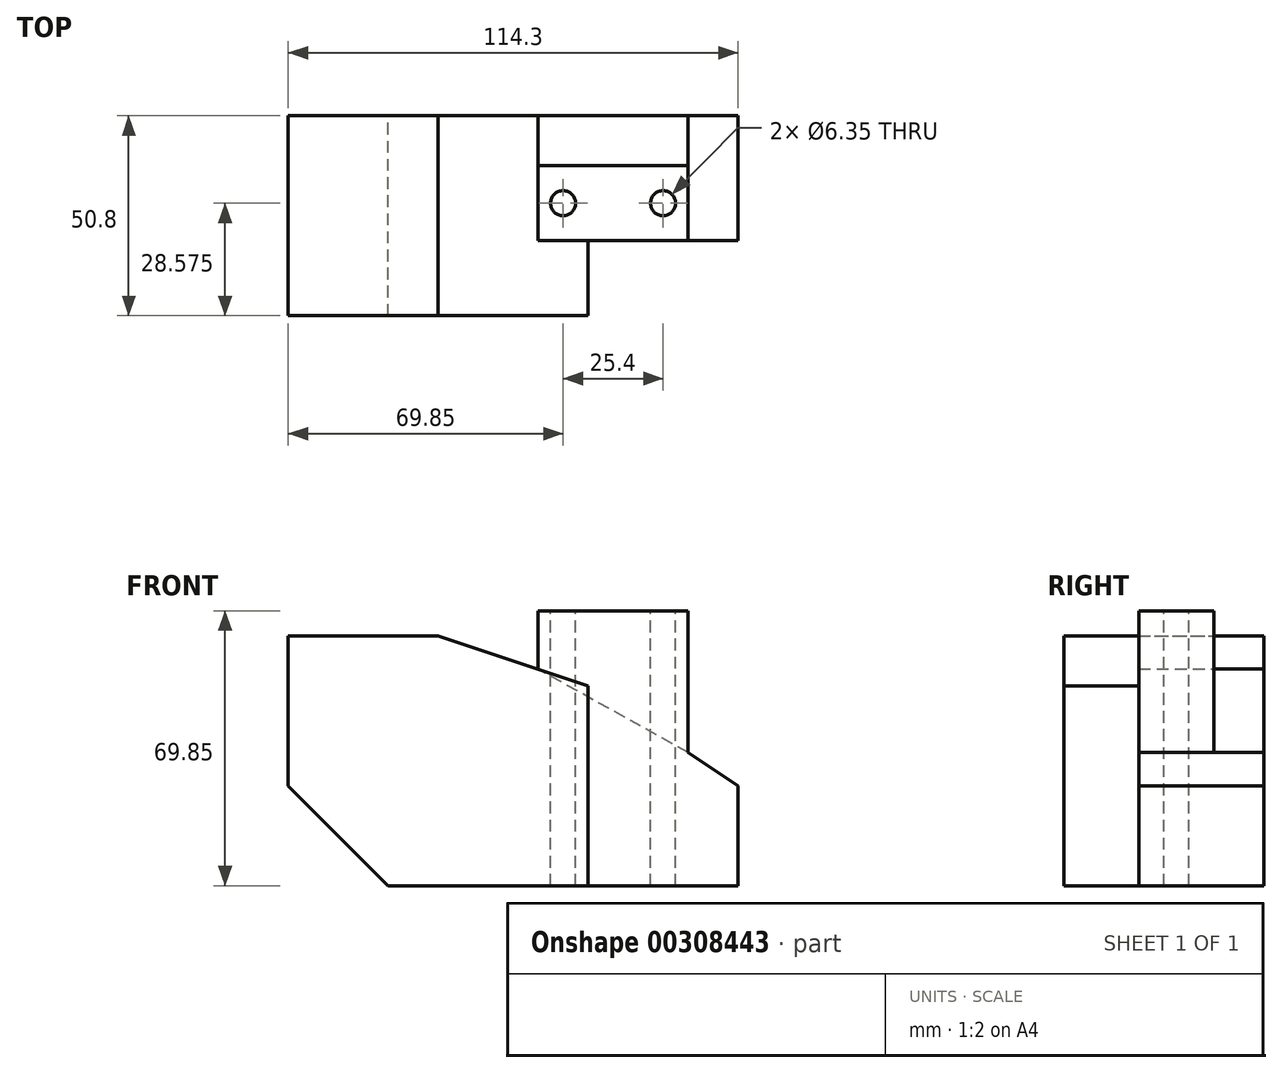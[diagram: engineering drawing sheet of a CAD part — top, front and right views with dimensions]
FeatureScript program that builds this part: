
annotation { "Feature Type Name" : "Feature", "Feature Type Description" : "" }
export const myFeature = defineFeature(function(context is Context, id is Id, definition is map)
    precondition{}
    {
        {
            var Q0;
            Q0=qCreatedBy(makeId("Front.planeOp"),FACE);
            var sketch = newSketch(context, id + "F0", { "sketchPlane" : qUnion([Q0])});
            skLineSegment(sketch, "E0.bottom", {"start": v(25.4, 0) * mm, "end": v(76.2, 0) * mm});
            skLineSegment(sketch, "E0.top", {"start": v(0, 63.5) * mm, "end": v(38.1, 63.5) * mm});
            skLineSegment(sketch, "E0.left", {"start": v(0, 25.4) * mm, "end": v(0, 63.5) * mm});
            skLineSegment(sketch, "E0.right", {"start": v(76.2, 0) * mm, "end": v(76.2, 50.8) * mm});
            skLineSegment(sketch, "E1", {"start": v(38.1, 63.5) * mm, "end": v(76.2, 50.8) * mm});
            skPoint(sketch, "E2.orphan", {"position": v(76.2, 63.5) * mm});
            skLineSegment(sketch, "E3", {"start": v(0, 25.4) * mm, "end": v(25.4, 0) * mm});
            skPoint(sketch, "E4.orphan", {"position": v(0, 0) * mm});
            skSolve(sketch);
        }
        {
            var Q0;
            Q0 = qSketchRegion(id + "F0", true);
            extrude(context, id + "F1", {"entities" : qUnion([Q0]), "depth" : 50.8 * mm});
        }
        {
            var Q0;
            Q0=qCreatedBy(makeId("Front.planeOp"),FACE);
            var sketch = newSketch(context, id + "F2", { "sketchPlane" : qUnion([Q0])});
            skLineSegment(sketch, "E5", {"start": v(63.5, 55.03) * mm, "end": v(63.5, 69.85) * mm});
            skLineSegment(sketch, "E6", {"start": v(63.5, 69.85) * mm, "end": v(101.6, 69.85) * mm});
            skLineSegment(sketch, "E7", {"start": v(101.6, 69.85) * mm, "end": v(101.6, 31.75) * mm});
            skLineSegment(sketch, "E8", {"start": v(101.6, 31.75) * mm, "end": v(76.2, 31.75) * mm});
            skLineSegment(sketch, "E9", {"start": v(76.2, 31.75) * mm, "end": v(76.2, 50.8) * mm});
            skLineSegment(sketch, "E10", {"start": v(76.2, 50.8) * mm, "end": v(63.5, 55.03) * mm});
            skSolve(sketch);
        }
        {
            var Q0;
            Q0 = qSketchRegion(id + "F2", true);
            extrude(context, id + "F3", {"entities" : qUnion([Q0]), "operationType" : NewBodyOperationType.ADD, "depth" : 31.75 * mm});
        }
        {
            var Q0;
            Q0=qCreatedBy(makeId("Front.planeOp"),FACE);
            var sketch = newSketch(context, id + "F4", { "sketchPlane" : qUnion([Q0])});
            skLineSegment(sketch, "E11", {"start": v(76.2, 50.8) * mm, "end": v(114.3, 25.4) * mm});
            skLineSegment(sketch, "E12", {"start": v(76.2, 0) * mm, "end": v(114.3, 0) * mm});
            skLineSegment(sketch, "E13", {"start": v(114.3, 0) * mm, "end": v(114.3, 25.4) * mm});
            skLineSegment(sketch, "E14", {"start": v(76.2, 50.8) * mm, "end": v(76.2, 0) * mm});
            skSolve(sketch);
        }
        {
            var Q0;
            Q0 = qSketchRegion(id + "F4", true);
            extrude(context, id + "F5", {"entities" : qUnion([Q0]), "operationType" : NewBodyOperationType.ADD, "depth" : 31.75 * mm});
        }
        {
            var Q0;
            Q0=makeQuery(id+"F5.boolean.opBoolean","MERGE",FACE,{"derivedFrom":[makeQuery(id+"F3.boolean.opBoolean","MERGE",FACE,{"derivedFrom":[makeQuery(id+"F1.opExtrude","CAP_FACE",FACE,{"disambiguationData":[OSD([sQuery(id+"F0.wireOp",EDGE,"E0.bottom"),sQuery(id+"F0.wireOp",EDGE,"E0.top"),sQuery(id+"F0.wireOp",EDGE,"E0.left"),sQuery(id+"F0.wireOp",EDGE,"E0.right"),sQuery(id+"F0.wireOp",EDGE,"E1"),sQuery(id+"F0.wireOp",EDGE,"E3")])],"isStart":true}),makeQuery(id+"F3.opExtrude","CAP_FACE",FACE,{"disambiguationData":[OSD([sQuery(id+"F2.wireOp",EDGE,"E5"),sQuery(id+"F2.wireOp",EDGE,"E6"),sQuery(id+"F2.wireOp",EDGE,"E7"),sQuery(id+"F2.wireOp",EDGE,"E8"),sQuery(id+"F2.wireOp",EDGE,"E9"),sQuery(id+"F2.wireOp",EDGE,"E10")])],"isStart":true})]}),makeQuery(id+"F5.opExtrude","CAP_FACE",FACE,{"disambiguationData":[OSD([sQuery(id+"F4.wireOp",EDGE,"E11"),sQuery(id+"F4.wireOp",EDGE,"E12"),sQuery(id+"F4.wireOp",EDGE,"E13"),sQuery(id+"F4.wireOp",EDGE,"E14")])],"isStart":true})]});
            var sketch = newSketch(context, id + "F6", { "sketchPlane" : qUnion([Q0])});
            skLineSegment(sketch, "E15", {"start": v(-101.6, 33.87) * mm, "end": v(-63.5, 55.03) * mm});
            skLineSegment(sketch, "E16", {"start": v(-101.6, 33.87) * mm, "end": v(-101.6, 69.85) * mm});
            skLineSegment(sketch, "E17", {"start": v(-101.6, 69.85) * mm, "end": v(-63.5, 69.85) * mm});
            skLineSegment(sketch, "E18", {"start": v(-63.5, 69.85) * mm, "end": v(-63.5, 55.03) * mm});
            skSolve(sketch);
        }
        {
            var Q0;
            Q0 = qSketchRegion(id + "F6", true);
            extrude(context, id + "F7", {"entities" : qUnion([Q0]), "operationType" : NewBodyOperationType.REMOVE, "oppositeDirection" : true, "depth" : 12.7 * mm});
        }
        {
            var Q0;
            Q0=makeQuery(id+"F3.opExtrude","SWEPT_FACE",FACE,{"disambiguationData":[OSD([sQuery(id+"F2.wireOp",EDGE,"E6")])]});
            var sketch = newSketch(context, id + "F8", { "sketchPlane" : qUnion([Q0])});
            skCircle(sketch, "E19", {"center": v(69.85, -22.23) * mm, "radius": 3.18 * mm});
            skPoint(sketch, "E19.centerSnap0", {"position": v(63.5, -22.23) * mm});
            skCircle(sketch, "E20", {"center": v(95.25, -22.22) * mm, "radius": 3.18 * mm});
            skSolve(sketch);
        }
        {
            var Q0;
            Q0 = qSketchRegion(id + "F8", true);
            extrude(context, id + "F9", {"entities" : qUnion([Q0]), "operationType" : NewBodyOperationType.REMOVE, "endBound" : BoundingType.THROUGH_ALL, "oppositeDirection" : true, "depth" : 25.4 * mm});
        }
    });
